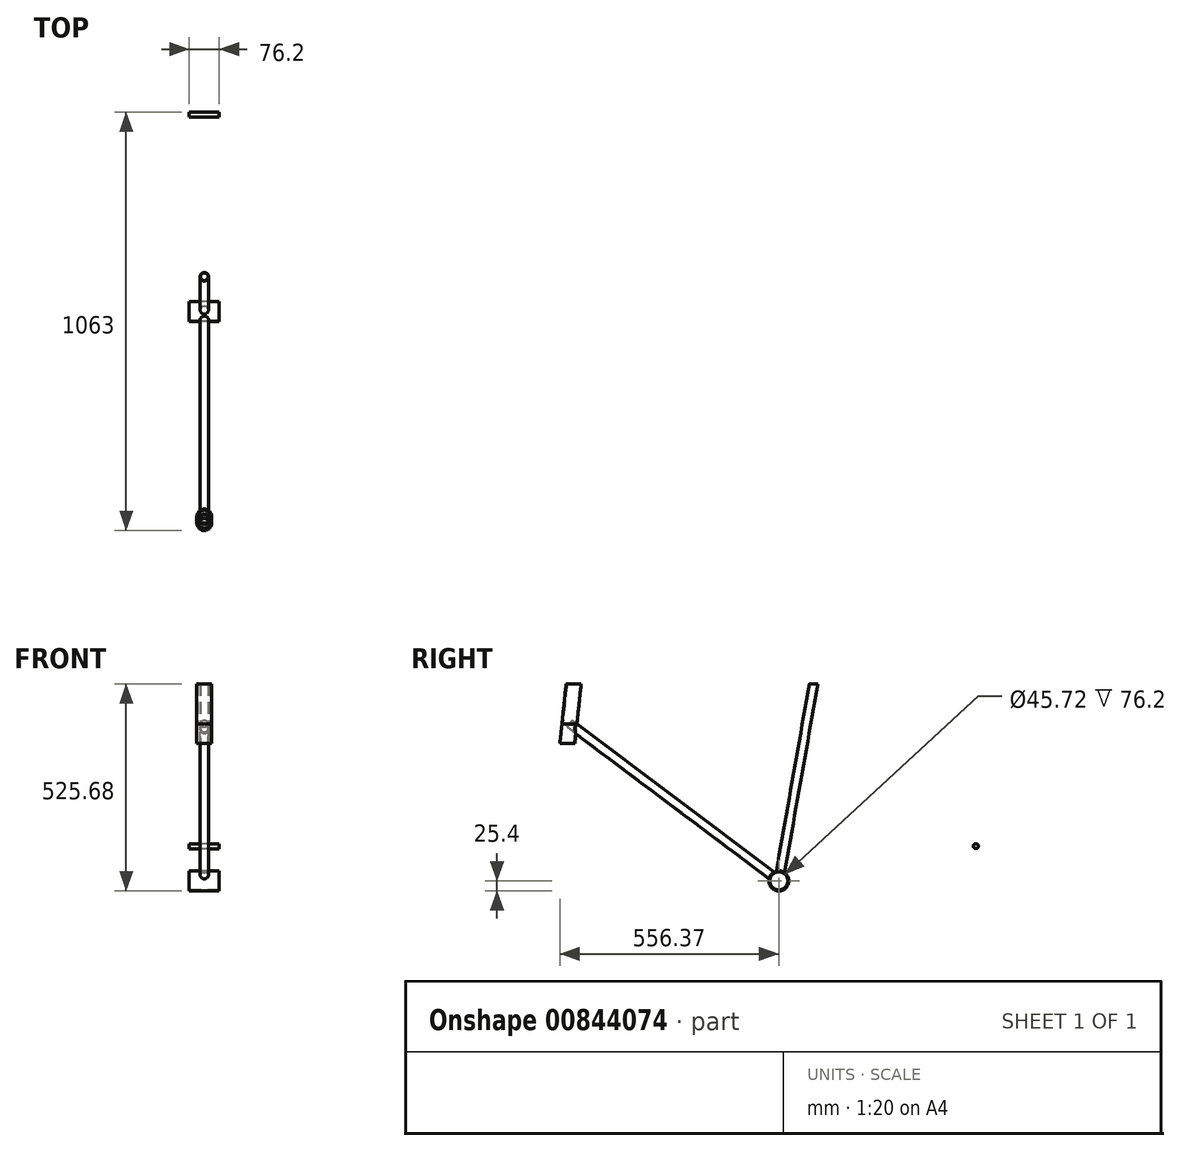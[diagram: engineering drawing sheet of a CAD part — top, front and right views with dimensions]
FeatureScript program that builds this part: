
annotation { "Feature Type Name" : "Feature", "Feature Type Description" : "" }
export const myFeature = defineFeature(function(context is Context, id is Id, definition is map)
    precondition{}
    {
        {
            var Q0;
            Q0=qCreatedBy(makeId("Right.planeOp"),FACE);
            var sketch = newSketch(context, id + "F0", { "sketchPlane" : qUnion([Q0])});
            skLineSegment(sketch, "E0", {"start": v(0, 0) * mm, "end": v(88.21, 500.28) * mm});
            skLineSegment(sketch, "E1", {"start": v(88.21, 500.28) * mm, "end": v(-521.39, 500.28) * mm});
            skLineSegment(sketch, "E2", {"start": v(-521.39, 500.28) * mm, "end": v(-532, 399.24) * mm});
            skLineSegment(sketch, "E3", {"start": v(-532, 399.24) * mm, "end": v(0, 0) * mm});
            skLineSegment(sketch, "E4", {"start": v(0, 0) * mm, "end": v(500.28, 88.21) * mm});
            skLineSegment(sketch, "E5", {"start": v(500.28, 88.21) * mm, "end": v(88.21, 500.28) * mm});
            skLineSegment(sketch, "E6", {"start": v(88.21, 500.28) * mm, "end": v(114.68, 650.37) * mm});
            skLineSegment(sketch, "E7", {"start": v(190.88, 650.37) * mm, "end": v(13.08, 650.37) * mm});
            skCircle(sketch, "E8", {"center": v(0, 0) * mm, "radius": 25.4 * mm});
            skCircle(sketch, "E9", {"center": v(0, 0) * mm, "radius": 22.86 * mm});
            skCircle(sketch, "E10", {"center": v(500.28, 88.21) * mm, "radius": 6.35 * mm});
            skLineSegment(sketch, "E11", {"start": v(-3.81, 2.86) * mm, "end": v(0, 7.94) * mm});
            skLineSegment(sketch, "E12", {"start": v(0, 7.94) * mm, "end": v(2.5, 7.5) * mm});
            skLineSegment(sketch, "E13", {"start": v(2.5, 7.5) * mm, "end": v(3.7, 0.65) * mm});
            skLineSegment(sketch, "E14", {"start": v(3.7, 0.65) * mm, "end": v(0, 0) * mm});
            skLineSegment(sketch, "E15.bottom", {"start": v(-544.7, 399.24) * mm, "end": v(-519.3, 399.24) * mm});
            skLineSegment(sketch, "E15.top", {"start": v(-544.7, 396.7) * mm, "end": v(-519.3, 396.7) * mm});
            skLineSegment(sketch, "E15.left", {"start": v(-544.7, 399.24) * mm, "end": v(-544.7, 396.7) * mm});
            skLineSegment(sketch, "E15.right", {"start": v(-519.3, 399.24) * mm, "end": v(-519.3, 396.7) * mm});
            skLineSegment(sketch, "E16", {"start": v(-532, 399.24) * mm, "end": v(-537.32, 348.72) * mm});
            skLineSegment(sketch, "E17", {"start": v(86.3, 489.49) * mm, "end": v(-522.52, 489.49) * mm});
            skSolve(sketch);
        }
        {
            var Q0;
            {var subQ0=sQuery(id+"F0.wireOp",EDGE,"E9");var subQ1=sQuery(id+"F0.wireOp",EDGE,"E0");var subQ2=makeQuery(id+"F0.imprint","INTERSECT",VERTEX,{"derivedFrom":[subQ1,subQ0]});Q0=makeQuery(id+"F0.imprint","IMPRINT",FACE,{"disambiguationData":[TD([[makeQuery(id+"F0.imprint","IMPRINT",EDGE,{"disambiguationData":[TD([[subQ2,-1.0]])],"derivedFrom":subQ1}),-1.0]])]});}
            var Q1;
            {var subQ0=sQuery(id+"F0.wireOp",EDGE,"E9");var subQ1=sQuery(id+"F0.wireOp",EDGE,"E0");var subQ2=makeQuery(id+"F0.imprint","INTERSECT",VERTEX,{"derivedFrom":[subQ1,subQ0]});Q1=makeQuery(id+"F0.imprint","IMPRINT",FACE,{"disambiguationData":[TD([[makeQuery(id+"F0.imprint","IMPRINT",EDGE,{"disambiguationData":[TD([[subQ2,-1.0]])],"derivedFrom":subQ1}),1.0]])]});}
            var Q2;
            {var subQ0=sQuery(id+"F0.wireOp",EDGE,"E8");var subQ1=sQuery(id+"F0.wireOp",EDGE,"E3");var subQ2=makeQuery(id+"F0.imprint","INTERSECT",VERTEX,{"derivedFrom":[subQ1,subQ0]});Q2=makeQuery(id+"F0.imprint","IMPRINT",FACE,{"disambiguationData":[TD([[makeQuery(id+"F0.imprint","IMPRINT",EDGE,{"disambiguationData":[TD([[subQ2,-1.0]])],"derivedFrom":subQ1}),-1.0]])]});}
            extrude(context, id + "F1", {"entities" : qUnion([Q0, Q1, Q2]), "endBound" : BoundingType.SYMMETRIC, "depth" : 76.2 * mm, "offsetDistance" : 25.4 * mm});
        }
        {
            var Q0;
            Q0=qCreatedBy(makeId("Top.planeOp"),FACE);
            var sketch = newSketch(context, id + "F2", { "sketchPlane" : qUnion([Q0])});
            skCircle(sketch, "E18", {"center": v(0, 0) * mm, "radius": 10.8 * mm});
            skCircle(sketch, "E19", {"center": v(0, 0) * mm, "radius": 9.53 * mm});
            skSolve(sketch);
        }
        {
            var Q0;
            Q0=makeQuery(id+"F2.imprint","IMPRINT",FACE,{"disambiguationData":[TD([[makeQuery(id+"F2.imprint","IMPRINT",EDGE,{"derivedFrom":sQuery(id+"F2.wireOp",EDGE,"E18")}),1.0]])]});
            var Q1;
            Q1=sQuery(id+"F0.wireOp",EDGE,"E0");
            sweep(context, id + "F3", {"operationType" : NewBodyOperationType.ADD, "profiles" : qUnion([Q0]), "path" : qUnion([Q1])});
        }
        {
            var Q0;
            {var subQ5=sQuery(id+"F0.wireOp",EDGE,"E11");Q0=makeQuery(id+"F0.imprint","IMPRINT",FACE,{"disambiguationData":[TD([[makeQuery(id+"F0.imprint","IMPRINT",EDGE,{"derivedFrom":subQ5}),-1.0]])]});}
            var Q1;
            {var subQ4=sQuery(id+"F0.wireOp",EDGE,"E13");Q1=makeQuery(id+"F0.imprint","IMPRINT",FACE,{"disambiguationData":[TD([[makeQuery(id+"F0.imprint","IMPRINT",EDGE,{"derivedFrom":subQ4}),-1.0]])]});}
            extrude(context, id + "F4", {"entities" : qUnion([Q0, Q1]), "endBound" : BoundingType.SYMMETRIC, "depth" : 25.4 * mm, "offsetDistance" : 25.4 * mm});
        }
        {
            var Q0;
            Q0=makeQuery(id+"F4.opExtrude","SWEPT_FACE",FACE,{"disambiguationData":[OSD([sQuery(id+"F0.wireOp",EDGE,"E11")])]});
            var sketch = newSketch(context, id + "F5", { "sketchPlane" : qUnion([Q0])});
            skCircle(sketch, "E20", {"center": v(0, 0) * mm, "radius": 10.8 * mm});
            skCircle(sketch, "E21", {"center": v(0, 0) * mm, "radius": 9.53 * mm});
            skSolve(sketch);
        }
        {
            var Q0;
            {var subQ0=sQuery(id+"F5.wireOp",EDGE,"E20");var subQ1=makeQuery(id+"F4.opExtrude","SWEPT_EDGE",EDGE,{"disambiguationData":[OSD([sQuery(id+"F0.wireOp",EDGE,"E3"),sQuery(id+"F0.wireOp",EDGE,"E11")])]});var subQ2=makeQuery(id+"F5.imprint","INTERSECT",VERTEX,{"disambiguationData":[OD(0.0)],"derivedFrom":[subQ1,subQ0]});Q0=makeQuery(id+"F5.imprint","IMPRINT",FACE,{"disambiguationData":[TD([[makeQuery(id+"F5.imprint","IMPRINT",EDGE,{"disambiguationData":[TD([[subQ2,1.0]])],"derivedFrom":subQ0}),1.0]])]});}
            var Q1;
            {var subQ0=sQuery(id+"F5.wireOp",EDGE,"E20");var subQ1=sQuery(id+"F0.wireOp",EDGE,"E11");var subQ2=makeQuery(id+"F4.opExtrude","SWEPT_EDGE",EDGE,{"disambiguationData":[OSD([subQ1,sQuery(id+"F0.wireOp",EDGE,"E12")])]});var subQ3=makeQuery(id+"F5.imprint","INTERSECT",VERTEX,{"disambiguationData":[OD(0.0)],"derivedFrom":[subQ2,subQ0]});Q1=makeQuery(id+"F5.imprint","IMPRINT",FACE,{"disambiguationData":[TD([[makeQuery(id+"F5.imprint","IMPRINT",EDGE,{"disambiguationData":[TD([[subQ3,1.0]])],"derivedFrom":subQ0}),1.0]])]});}
            var Q2;
            {var subQ0=sQuery(id+"F5.wireOp",EDGE,"E20");var subQ1=makeQuery(id+"F4.opExtrude","SWEPT_EDGE",EDGE,{"disambiguationData":[OSD([sQuery(id+"F0.wireOp",EDGE,"E11"),sQuery(id+"F0.wireOp",EDGE,"E12")])]});var subQ2=makeQuery(id+"F5.imprint","INTERSECT",VERTEX,{"disambiguationData":[OD(0.0)],"derivedFrom":[subQ1,subQ0]});Q2=makeQuery(id+"F5.imprint","IMPRINT",FACE,{"disambiguationData":[TD([[makeQuery(id+"F5.imprint","IMPRINT",EDGE,{"disambiguationData":[TD([[subQ2,-1.0]])],"derivedFrom":subQ0}),1.0]])]});}
            var Q3;
            {var subQ0=sQuery(id+"F5.wireOp",EDGE,"E20");var subQ1=sQuery(id+"F0.wireOp",EDGE,"E11");var subQ2=makeQuery(id+"F4.opExtrude","SWEPT_EDGE",EDGE,{"disambiguationData":[OSD([subQ1,sQuery(id+"F0.wireOp",EDGE,"E12")])]});var subQ3=makeQuery(id+"F5.imprint","INTERSECT",VERTEX,{"disambiguationData":[OD(1.0)],"derivedFrom":[subQ2,subQ0]});Q3=makeQuery(id+"F5.imprint","IMPRINT",FACE,{"disambiguationData":[TD([[makeQuery(id+"F5.imprint","IMPRINT",EDGE,{"disambiguationData":[TD([[subQ3,-1.0]])],"derivedFrom":subQ0}),1.0]])]});}
            var Q4;
            Q4=sQuery(id+"F0.wireOp",EDGE,"E3");
            sweep(context, id + "F6", {"operationType" : NewBodyOperationType.ADD, "profiles" : qUnion([Q0, Q1, Q2, Q3]), "path" : qUnion([Q4])});
        }
        {
            var Q0;
            {var subQ1=sQuery(id+"F0.wireOp",EDGE,"E3");var subQ3=sQuery(id+"F0.wireOp",EDGE,"E9");var subQ4=makeQuery(id+"F0.imprint","INTERSECT",VERTEX,{"derivedFrom":[subQ1,subQ3]});Q0=makeQuery(id+"F0.imprint","IMPRINT",FACE,{"disambiguationData":[TD([[makeQuery(id+"F0.imprint","IMPRINT",EDGE,{"disambiguationData":[TD([[subQ4,-1.0]])],"derivedFrom":subQ3}),1.0]])]});}
            var Q1;
            {var subQ1=sQuery(id+"F0.wireOp",EDGE,"E0");var subQ3=sQuery(id+"F0.wireOp",EDGE,"E9");var subQ4=makeQuery(id+"F0.imprint","INTERSECT",VERTEX,{"derivedFrom":[subQ1,subQ3]});Q1=makeQuery(id+"F0.imprint","IMPRINT",FACE,{"disambiguationData":[TD([[makeQuery(id+"F0.imprint","IMPRINT",EDGE,{"disambiguationData":[TD([[subQ4,1.0]])],"derivedFrom":subQ3}),1.0]])]});}
            var Q2;
            {var subQ1=sQuery(id+"F0.wireOp",EDGE,"E0");var subQ3=sQuery(id+"F0.wireOp",EDGE,"E9");var subQ4=makeQuery(id+"F0.imprint","INTERSECT",VERTEX,{"derivedFrom":[subQ1,subQ3]});Q2=makeQuery(id+"F0.imprint","IMPRINT",FACE,{"disambiguationData":[TD([[makeQuery(id+"F0.imprint","IMPRINT",EDGE,{"disambiguationData":[TD([[subQ4,-1.0]])],"derivedFrom":subQ3}),1.0]])]});}
            var Q3;
            {var subQ4=sQuery(id+"F0.wireOp",EDGE,"E13");Q3=makeQuery(id+"F0.imprint","IMPRINT",FACE,{"disambiguationData":[TD([[makeQuery(id+"F0.imprint","IMPRINT",EDGE,{"derivedFrom":subQ4}),-1.0]])]});}
            var Q4;
            {var subQ5=sQuery(id+"F0.wireOp",EDGE,"E11");Q4=makeQuery(id+"F0.imprint","IMPRINT",FACE,{"disambiguationData":[TD([[makeQuery(id+"F0.imprint","IMPRINT",EDGE,{"derivedFrom":subQ5}),-1.0]])]});}
            extrude(context, id + "F7", {"entities" : qUnion([Q0, Q1, Q2, Q3, Q4]), "operationType" : NewBodyOperationType.REMOVE, "endBound" : BoundingType.SYMMETRIC, "oppositeDirection" : true, "depth" : 25.4 * mm, "offsetDistance" : 25.4 * mm});
        }
        {
            var Q0;
            {var subQ0=sQuery(id+"F0.wireOp",EDGE,"E5");var subQ1=sQuery(id+"F0.wireOp",EDGE,"E4");var subQ2=makeQuery(id+"F0.imprint","INTERSECT",VERTEX,{"derivedFrom":[subQ1,subQ0]});Q0=makeQuery(id+"F0.imprint","IMPRINT",FACE,{"disambiguationData":[TD([[makeQuery(id+"F0.imprint","IMPRINT",EDGE,{"disambiguationData":[TD([[subQ2,1.0]])],"derivedFrom":subQ1}),1.0]])]});}
            var Q1;
            {var subQ0=sQuery(id+"F0.wireOp",EDGE,"E5");var subQ1=sQuery(id+"F0.wireOp",EDGE,"E4");var subQ2=makeQuery(id+"F0.imprint","INTERSECT",VERTEX,{"derivedFrom":[subQ1,subQ0]});Q1=makeQuery(id+"F0.imprint","IMPRINT",FACE,{"disambiguationData":[TD([[makeQuery(id+"F0.imprint","IMPRINT",EDGE,{"disambiguationData":[TD([[subQ2,1.0]])],"derivedFrom":subQ1}),-1.0]])]});}
            extrude(context, id + "F8", {"entities" : qUnion([Q0, Q1]), "endBound" : BoundingType.SYMMETRIC, "depth" : 76.2 * mm, "offsetDistance" : 25.4 * mm});
        }
        {
            var Q0;
            {var subQ5=sQuery(id+"F0.wireOp",EDGE,"E15.left");Q0=makeQuery(id+"F0.imprint","IMPRINT",FACE,{"disambiguationData":[TD([[makeQuery(id+"F0.imprint","IMPRINT",EDGE,{"derivedFrom":subQ5}),1.0]])]});}
            var Q1;
            {var subQ5=sQuery(id+"F0.wireOp",EDGE,"E15.right");Q1=makeQuery(id+"F0.imprint","IMPRINT",FACE,{"disambiguationData":[TD([[makeQuery(id+"F0.imprint","IMPRINT",EDGE,{"derivedFrom":subQ5}),-1.0]])]});}
            var Q2;
            {var subQ0=sQuery(id+"F0.wireOp",EDGE,"E16");var subQ3=sQuery(id+"F0.wireOp",EDGE,"E15.top");var subQ5=makeQuery(id+"F0.imprint","INTERSECT",VERTEX,{"derivedFrom":[subQ3,subQ0]});Q2=makeQuery(id+"F0.imprint","IMPRINT",FACE,{"disambiguationData":[TD([[makeQuery(id+"F0.imprint","IMPRINT",EDGE,{"disambiguationData":[TD([[subQ5,-1.0]])],"derivedFrom":subQ3}),1.0]])]});}
            extrude(context, id + "F9", {"entities" : qUnion([Q0, Q1, Q2]), "endBound" : BoundingType.SYMMETRIC, "depth" : 25.4 * mm, "offsetDistance" : 25.4 * mm});
        }
        {
            var Q0;
            Q0=makeQuery(id+"F9.opExtrude","SWEPT_FACE",FACE,{"disambiguationData":[OSD([sQuery(id+"F0.wireOp",EDGE,"E15.bottom")])]});
            var sketch = newSketch(context, id + "F10", { "sketchPlane" : qUnion([Q0])});
            skCircle(sketch, "E22", {"center": v(0, -532) * mm, "radius": 19.05 * mm});
            skPoint(sketch, "E22.centerSnap0", {"position": v(12.7, -532) * mm});
            skCircle(sketch, "E23.0", {"center": v(0, -532) * mm, "radius": 16.51 * mm});
            skSolve(sketch);
        }
        {
            var Q0;
            Q0=makeQuery(id+"F10.imprint","IMPRINT",FACE,{"disambiguationData":[TD([[makeQuery(id+"F10.imprint","IMPRINT",EDGE,{"derivedFrom":sQuery(id+"F10.wireOp",EDGE,"E22")}),1.0]])]});
            var Q1;
            {var subQ0=sQuery(id+"F10.wireOp",EDGE,"E23.0");var subQ1=sQuery(id+"F0.wireOp",EDGE,"E15.bottom");var subQ4=makeQuery(id+"F9.opExtrude","CAP_EDGE",EDGE,{"disambiguationData":[OSD([subQ1])],"isStart":false});var subQ5=makeQuery(id+"F10.imprint","INTERSECT",VERTEX,{"disambiguationData":[OD(0.0)],"derivedFrom":[subQ4,subQ0]});Q1=makeQuery(id+"F10.imprint","IMPRINT",FACE,{"disambiguationData":[TD([[makeQuery(id+"F10.imprint","IMPRINT",EDGE,{"disambiguationData":[TD([[subQ5,-1.0]])],"derivedFrom":subQ0}),-1.0]])]});}
            var Q2;
            {var subQ0=sQuery(id+"F10.wireOp",EDGE,"E23.0");var subQ1=sQuery(id+"F0.wireOp",EDGE,"E15.bottom");var subQ4=makeQuery(id+"F9.opExtrude","CAP_EDGE",EDGE,{"disambiguationData":[OSD([subQ1])],"isStart":false});var subQ5=makeQuery(id+"F10.imprint","INTERSECT",VERTEX,{"disambiguationData":[OD(1.0)],"derivedFrom":[subQ4,subQ0]});Q2=makeQuery(id+"F10.imprint","IMPRINT",FACE,{"disambiguationData":[TD([[makeQuery(id+"F10.imprint","IMPRINT",EDGE,{"disambiguationData":[TD([[subQ5,1.0]])],"derivedFrom":subQ0}),-1.0]])]});}
            var Q3;
            {var subQ0=sQuery(id+"F10.wireOp",EDGE,"E23.0");var subQ1=sQuery(id+"F0.wireOp",EDGE,"E15.bottom");var subQ2=makeQuery(id+"F9.opExtrude","CAP_EDGE",EDGE,{"disambiguationData":[OSD([subQ1])],"isStart":true});var subQ3=makeQuery(id+"F10.imprint","INTERSECT",VERTEX,{"disambiguationData":[OD(1.0)],"derivedFrom":[subQ2,subQ0]});Q3=makeQuery(id+"F10.imprint","IMPRINT",FACE,{"disambiguationData":[TD([[makeQuery(id+"F10.imprint","IMPRINT",EDGE,{"disambiguationData":[TD([[subQ3,-1.0]])],"derivedFrom":subQ0}),-1.0]])]});}
            var Q4;
            {var subQ0=sQuery(id+"F10.wireOp",EDGE,"E23.0");var subQ1=sQuery(id+"F0.wireOp",EDGE,"E15.bottom");var subQ4=makeQuery(id+"F9.opExtrude","CAP_EDGE",EDGE,{"disambiguationData":[OSD([subQ1])],"isStart":true});var subQ5=makeQuery(id+"F10.imprint","INTERSECT",VERTEX,{"disambiguationData":[OD(0.0)],"derivedFrom":[subQ4,subQ0]});Q4=makeQuery(id+"F10.imprint","IMPRINT",FACE,{"disambiguationData":[TD([[makeQuery(id+"F10.imprint","IMPRINT",EDGE,{"disambiguationData":[TD([[subQ5,1.0]])],"derivedFrom":subQ0}),-1.0]])]});}
            var Q5;
            Q5=sQuery(id+"F0.wireOp",EDGE,"E2");
            var Q6;
            Q6=sQuery(id+"F0.wireOp",EDGE,"E16");
            sweep(context, id + "F11", {"operationType" : NewBodyOperationType.ADD, "profiles" : qUnion([Q0, Q1, Q2, Q3, Q4]), "path" : qUnion([Q5, Q6])});
        }
    });
